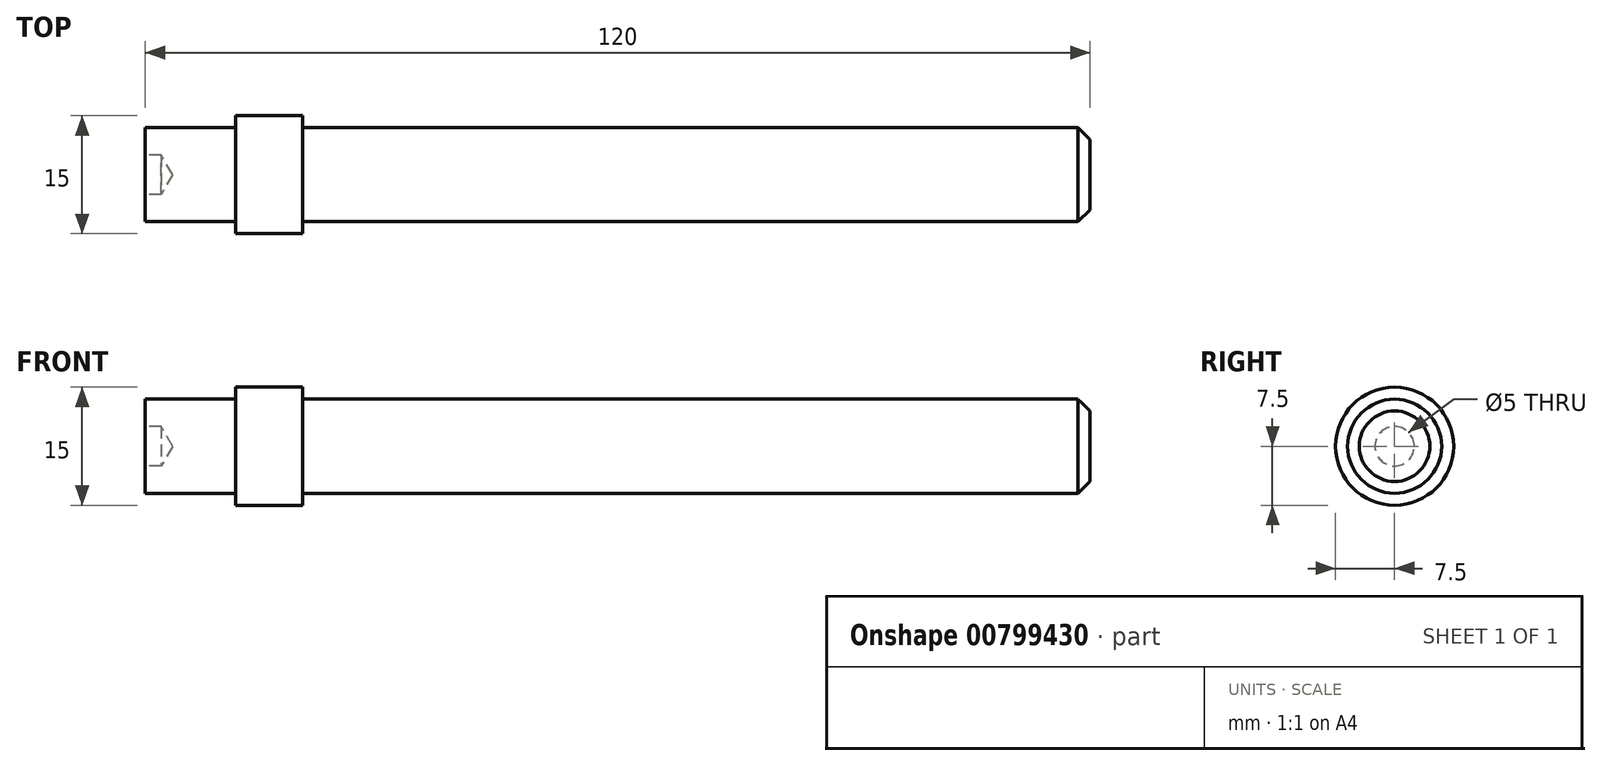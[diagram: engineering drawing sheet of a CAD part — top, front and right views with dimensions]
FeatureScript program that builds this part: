
annotation { "Feature Type Name" : "Feature", "Feature Type Description" : "" }
export const myFeature = defineFeature(function(context is Context, id is Id, definition is map)
    precondition{}
    {
        {
            var Q0;
            Q0=qCreatedBy(makeId("Front.planeOp"),FACE);
            var sketch = newSketch(context, id + "F0", { "sketchPlane" : qUnion([Q0])});
            skLineSegment(sketch, "E0", {"start": v(0, 0) * mm, "end": v(0, 5.98) * mm});
            skLineSegment(sketch, "E1", {"start": v(0, 5.98) * mm, "end": v(-100, 5.97) * mm});
            skLineSegment(sketch, "E2", {"start": v(-100, 5.97) * mm, "end": v(-100, 7.5) * mm});
            skLineSegment(sketch, "E3", {"start": v(-100, 7.5) * mm, "end": v(-108.5, 7.5) * mm});
            skLineSegment(sketch, "E4", {"start": v(-108.5, 7.5) * mm, "end": v(-108.5, 5.98) * mm});
            skLineSegment(sketch, "E5", {"start": v(-108.5, 5.98) * mm, "end": v(-120, 5.97) * mm});
            skLineSegment(sketch, "E6", {"start": v(-120, 5.97) * mm, "end": v(-120, 0) * mm});
            skLineSegment(sketch, "E7", {"start": v(-120, 0) * mm, "end": v(0, 0) * mm});
            skSolve(sketch);
        }
        {
            var Q0;
            Q0=makeQuery(id+"F0.imprint","IMPRINT",FACE,{"disambiguationData":[TD([[makeQuery(id+"F0.imprint","IMPRINT",EDGE,{"derivedFrom":sQuery(id+"F0.wireOp",EDGE,"E0")}),1.0]])]});
            var Q1;
            Q1=sQuery(id+"F0.wireOp",EDGE,"E7");
            revolve(context, id + "F1", {"surfaceOperationType" : NewSurfaceOperationType.NEW, "entities" : qUnion([Q0]), "axis" : qUnion([Q1]), "revolveType" : RevolveType.FULL});
        }
        {
            var Q0;
            Q0=makeQuery(id+"F1.opRevolve","SWEPT_FACE",FACE,{"disambiguationData":[OSD([sQuery(id+"F0.wireOp",EDGE,"E6")])]});
            var sketch = newSketch(context, id + "F2", { "sketchPlane" : qUnion([Q0])});
            skPoint(sketch, "E8", {"position": v(0, 0) * mm});
            skSolve(sketch);
        }
        {
            var Q0;
            Q0=sQuery(id+"F2.wireOp",VERTEX,"E8");
            var Q1;
            Q1=makeQuery(id+"F1.opRevolve","SWEPT_BODY",BODY,{"disambiguationData":[OSD([sQuery(id+"F0.wireOp",EDGE,"E0"),sQuery(id+"F0.wireOp",EDGE,"E1"),sQuery(id+"F0.wireOp",EDGE,"E2"),sQuery(id+"F0.wireOp",EDGE,"E3"),sQuery(id+"F0.wireOp",EDGE,"E4"),sQuery(id+"F0.wireOp",EDGE,"E5"),sQuery(id+"F0.wireOp",EDGE,"E6"),sQuery(id+"F0.wireOp",EDGE,"E7")])]});
            hole(context, id + "F3", {"style" : HoleStyle.SIMPLE, "endStyle" : HoleEndStyle.BLIND, "holeDiameter" : 5 * mm, "majorDiameter" : 5 * mm, "holeDepth" : 2 * mm, "isTappedThrough" : true, "tappedDepth" : 12 * mm, "tapClearance" : 3, "locations" : qUnion([Q0]), "scope" : qUnion([Q1])});
        }
        {
            var Q0;
            Q0=makeQuery(id+"F1.opRevolve","SWEPT_EDGE",EDGE,{"disambiguationData":[OSD([sQuery(id+"F0.wireOp",EDGE,"E0"),sQuery(id+"F0.wireOp",EDGE,"E1")])]});
            chamfer(context, id + "F4", {"entities" : qUnion([Q0]), "width" : 1.5 * mm, "tangentPropagation" : true});
        }
    });
